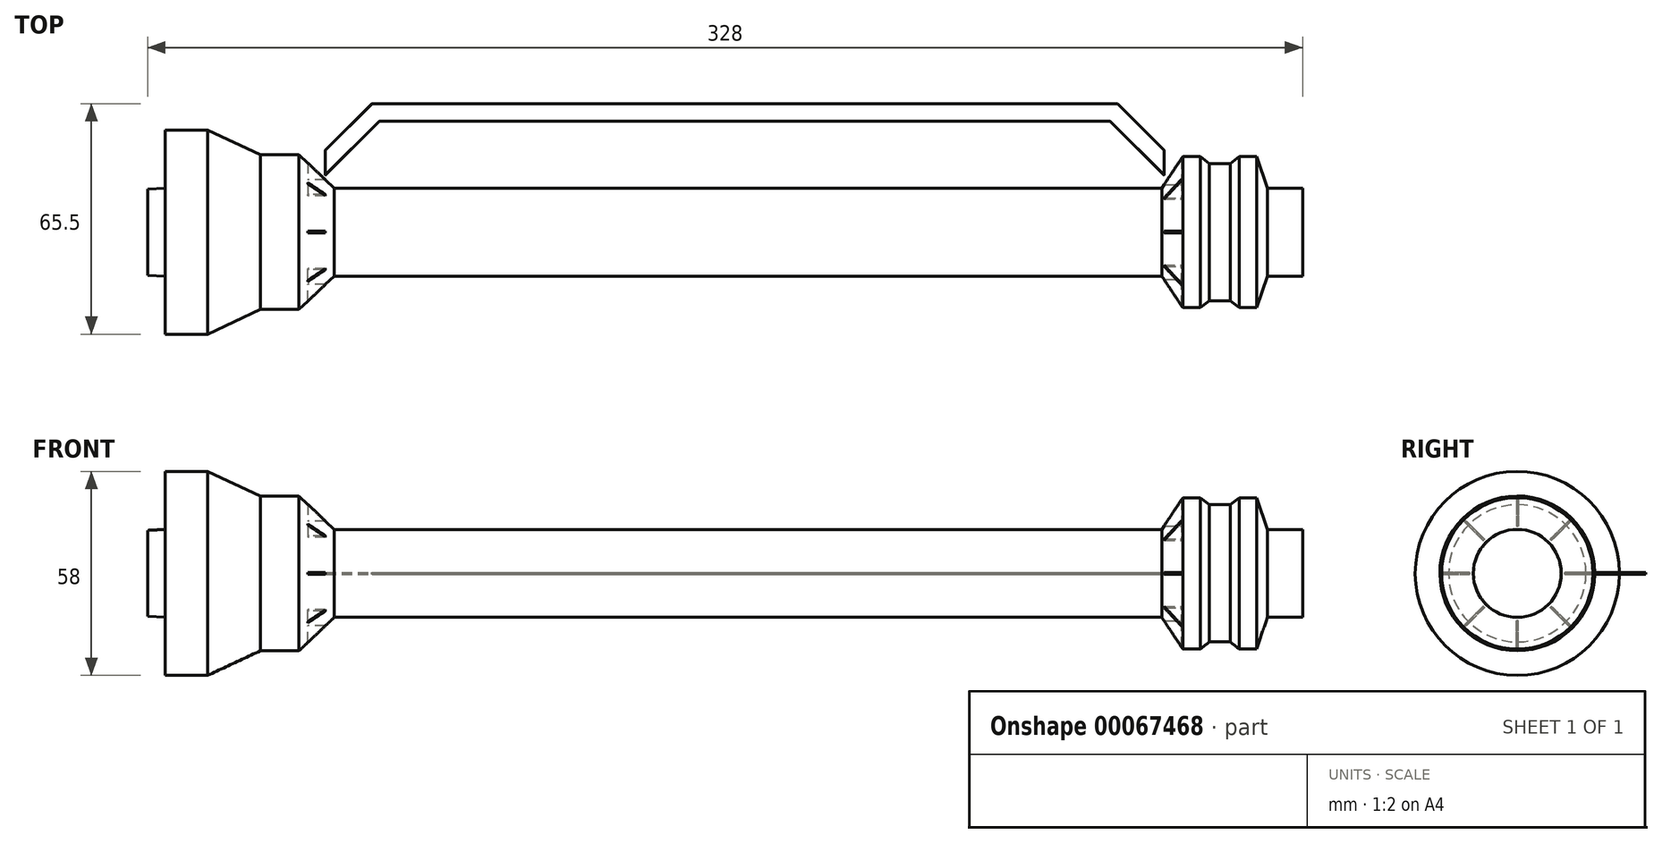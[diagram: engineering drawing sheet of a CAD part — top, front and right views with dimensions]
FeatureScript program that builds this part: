
annotation { "Feature Type Name" : "Feature", "Feature Type Description" : "" }
export const myFeature = defineFeature(function(context is Context, id is Id, definition is map)
    precondition{}
    {
        {
            assignVariable(context, id + "F0", {"name" : "s", "anyValue" : 1});
        }
        {
            var Q0;
            Q0=qCreatedBy(makeId("Top.planeOp"),FACE);
            var sketch = newSketch(context, id + "F1", { "sketchPlane" : qUnion([Q0])});
            skLineSegment(sketch, "E0", {"start": v(0, 0) * mm, "end": v(0, 29) * mm});
            skLineSegment(sketch, "E1", {"start": v(0, 29) * mm, "end": v(12, 29) * mm});
            skLineSegment(sketch, "E2", {"start": v(12, 29) * mm, "end": v(27, 22) * mm});
            skLineSegment(sketch, "E3", {"start": v(27, 22) * mm, "end": v(38, 22) * mm});
            skLineSegment(sketch, "E4", {"start": v(38, 22) * mm, "end": v(48, 12.5) * mm});
            skLineSegment(sketch, "E5", {"start": v(48, 12.5) * mm, "end": v(283, 12.5) * mm});
            skLineSegment(sketch, "E6", {"start": v(283, 12.5) * mm, "end": v(289, 21.5) * mm});
            skLineSegment(sketch, "E7", {"start": v(289, 21.5) * mm, "end": v(294, 21.5) * mm});
            skLineSegment(sketch, "E8", {"start": v(294, 21.5) * mm, "end": v(296.5, 19.5) * mm});
            skLineSegment(sketch, "E9", {"start": v(296.5, 19.5) * mm, "end": v(302.5, 19.5) * mm});
            skLineSegment(sketch, "E10", {"start": v(302.5, 19.5) * mm, "end": v(305, 21.5) * mm});
            skLineSegment(sketch, "E11", {"start": v(305, 21.5) * mm, "end": v(310, 21.5) * mm});
            skLineSegment(sketch, "E12", {"start": v(310, 21.5) * mm, "end": v(313, 12.5) * mm});
            skLineSegment(sketch, "E13", {"start": v(313, 12.5) * mm, "end": v(323, 12.5) * mm});
            skLineSegment(sketch, "E14", {"start": v(323, 12.5) * mm, "end": v(323, 0) * mm});
            skLineSegment(sketch, "E15", {"start": v(323, 0) * mm, "end": v(0, 0) * mm});
            skLineSegment(sketch, "E16", {"start": v(43, 17.25) * mm, "end": v(43, 14.87) * mm});
            skLineSegment(sketch, "E17", {"start": v(43, 14.87) * mm, "end": v(45.5, 14.87) * mm});
            skLineSegment(sketch, "E18", {"start": v(43, 14.87) * mm, "end": v(40.5, 14.87) * mm});
            skLineSegment(sketch, "E19", {"start": v(43, 17.25) * mm, "end": v(59.75, 34) * mm});
            skLineSegment(sketch, "E20", {"start": v(59.75, 34) * mm, "end": v(269.42, 34) * mm});
            skLineSegment(sketch, "E21", {"start": v(269.42, 34) * mm, "end": v(286.17, 17.25) * mm});
            skLineSegment(sketch, "E22", {"start": v(286.17, 17.25) * mm, "end": v(286.17, 13.5) * mm});
            skLineSegment(sketch, "E23", {"start": v(286.17, 13.5) * mm, "end": v(283.67, 13.5) * mm, "construction": true});
            skSolve(sketch);
        }
        {
            var Q0;
            Q0=makeQuery(id+"F1.imprint","IMPRINT",FACE,{"disambiguationData":[TD([[makeQuery(id+"F1.imprint","IMPRINT",EDGE,{"derivedFrom":sQuery(id+"F1.wireOp",EDGE,"E0")}),-1.0]])]});
            var Q1;
            {var subQ0=sQuery(id+"F1.wireOp",EDGE,"E16");Q1=makeQuery(id+"F1.imprint","IMPRINT",FACE,{"disambiguationData":[TD([[makeQuery(id+"F1.imprint","IMPRINT",EDGE,{"derivedFrom":subQ0}),1.0]])]});}
            var Q2;
            Q2=sQuery(id+"F1.wireOp",EDGE,"E15");
            revolve(context, id + "F2", {"entities" : qUnion([Q0, Q1]), "axis" : qUnion([Q2]), "revolveType" : RevolveType.SYMMETRIC, "angle" : 45 * degree});
        }
        {
            var Q0;
            Q0=sQuery(id+"F1.wireOp",EDGE,"E18");
            var Q1;
            Q1=sQuery(id+"F1.wireOp",EDGE,"E17");
            extrude(context, id + "F3", {"bodyType" : ToolBodyType.SURFACE, "surfaceEntities" : qUnion([Q0, Q1]), "endBound" : BoundingType.SYMMETRIC, "depth" : (0.5 * getVariable(context, 's')) * mm});
        }
        {
            var Q0;
            Q0=makeQuery(id+"F3.opExtrude","SWEPT_FACE",FACE,{"disambiguationData":[OSD([sQuery(id+"F1.wireOp",EDGE,"E17"),sQuery(id+"F1.wireOp",EDGE,"E18")])]});
            var sketch = newSketch(context, id + "F4", { "sketchPlane" : qUnion([Q0])});
            skCircle(sketch, "E24", {"center": v(-43, 0) * mm, "radius": 2.5 * mm});
            skPoint(sketch, "E24.centerSnap0", {"position": v(-45.5, 0) * mm});
            skPoint(sketch, "E24.centerSnap1", {"position": v(-43, 2.5) * mm});
            skSolve(sketch);
        }
        {
            var Q0;
            {var subQ0=sQuery(id+"F4.wireOp",EDGE,"E24");var subQ4=makeQuery(id+"F4.imprint","INTERSECT",VERTEX,{"derivedFrom":[makeQuery(id+"F3.opExtrude","SWEPT_EDGE",EDGE,{"disambiguationData":[OSD([sQuery(id+"F1.wireOp",VERTEX,"E18.end")])]}),subQ0]});Q0=makeQuery(id+"F4.imprint","IMPRINT",FACE,{"disambiguationData":[TD([[makeQuery(id+"F4.imprint","IMPRINT",EDGE,{"disambiguationData":[TD([[subQ4,-1.0]])],"derivedFrom":subQ0}),1.0]])]});}
            var Q1;
            Q1=sQuery(id+"F1.wireOp",EDGE,"E16");
            var Q2;
            Q2=sQuery(id+"F1.wireOp",EDGE,"E19");
            var Q3;
            Q3=sQuery(id+"F1.wireOp",EDGE,"E20");
            var Q4;
            Q4=sQuery(id+"F1.wireOp",EDGE,"E21");
            var Q5;
            Q5=sQuery(id+"F1.wireOp",EDGE,"E22");
            sweep(context, id + "F5", {"profiles" : qUnion([Q0]), "path" : qUnion([Q1, Q2, Q3, Q4, Q5])});
        }
        {
            var Q0;
            Q0=makeQuery(id+"F5.opSweep","CAP_FACE",FACE,{"disambiguationData":[OSD([sQuery(id+"F1.wireOp",VERTEX,"E16.end"),sQuery(id+"F4.wireOp",EDGE,"E24")])],"isStart":true});
            var Q1;
            Q1=makeQuery(id+"F5.opSweep","CAP_FACE",FACE,{"disambiguationData":[OSD([sQuery(id+"F1.wireOp",VERTEX,"E22.end"),sQuery(id+"F4.wireOp",EDGE,"E24")])],"isStart":false});
            extrude(context, id + "F6", {"entities" : qUnion([Q0, Q1]), "operationType" : NewBodyOperationType.REMOVE, "endBound" : BoundingType.THROUGH_ALL, "oppositeDirection" : true, "depth" : 25 * mm});
        }
        {
            var Q0;
            Q0=makeQuery(id+"F2.opRevolve","SWEPT_BODY",BODY,{"disambiguationData":[OSD([sQuery(id+"F1.wireOp",EDGE,"E0"),sQuery(id+"F1.wireOp",EDGE,"E1"),sQuery(id+"F1.wireOp",EDGE,"E2"),sQuery(id+"F1.wireOp",EDGE,"E3"),sQuery(id+"F1.wireOp",EDGE,"E4"),sQuery(id+"F1.wireOp",EDGE,"E5"),sQuery(id+"F1.wireOp",EDGE,"E6"),sQuery(id+"F1.wireOp",EDGE,"E7"),sQuery(id+"F1.wireOp",EDGE,"E8"),sQuery(id+"F1.wireOp",EDGE,"E9"),sQuery(id+"F1.wireOp",EDGE,"E10"),sQuery(id+"F1.wireOp",EDGE,"E11"),sQuery(id+"F1.wireOp",EDGE,"E12"),sQuery(id+"F1.wireOp",EDGE,"E13"),sQuery(id+"F1.wireOp",EDGE,"E14"),sQuery(id+"F1.wireOp",EDGE,"E15")])]});
            var Q1;
            Q1=makeQuery(id+"F2.opRevolve","CAP_EDGE",EDGE,{"disambiguationData":[OSD([sQuery(id+"F1.wireOp",EDGE,"E15")])],"isStart":true});
            circularPattern(context, id + "F7", {"operationType" : NewBodyOperationType.ADD, "entities" : qUnion([Q0]), "axis" : qUnion([Q1]), "angle" : 360 * degree, "instanceCount" : 8, "equalSpace" : true});
        }
        {
            var Q0;
            {var subQ0=makeQuery(id+"F2.opRevolve","SWEPT_FACE",FACE,{"disambiguationData":[OSD([sQuery(id+"F1.wireOp",EDGE,"E0")])]});Q0=makeQuery(id+"F7.boolean.opBoolean","MERGE",FACE,{"derivedFrom":[subQ0,makeQuery(id+"F7.opPattern","COPY",FACE,{"derivedFrom":subQ0,"instanceName":"1"}),makeQuery(id+"F7.opPattern","COPY",FACE,{"derivedFrom":subQ0,"instanceName":"2"}),makeQuery(id+"F7.opPattern","COPY",FACE,{"derivedFrom":subQ0,"instanceName":"3"}),makeQuery(id+"F7.opPattern","COPY",FACE,{"derivedFrom":subQ0,"instanceName":"4"}),makeQuery(id+"F7.opPattern","COPY",FACE,{"derivedFrom":subQ0,"instanceName":"5"}),makeQuery(id+"F7.opPattern","COPY",FACE,{"derivedFrom":subQ0,"instanceName":"6"}),makeQuery(id+"F7.opPattern","COPY",FACE,{"derivedFrom":subQ0,"instanceName":"7"})]});}
            var sketch = newSketch(context, id + "F8", { "sketchPlane" : qUnion([Q0])});
            skCircle(sketch, "E25.0", {"center": v(0, 0) * mm, "radius": 12.5 * mm});
            skSolve(sketch);
        }
        {
            var Q0;
            Q0 = qSketchRegion(id + "F8", true);
            extrude(context, id + "F9", {"entities" : qUnion([Q0]), "operationType" : NewBodyOperationType.ADD, "depth" : (5 * getVariable(context, 's')) * mm, "hasDraft" : true, "draftAngle" : 3 * degree, "draftPullDirection" : true});
        }
        {
            assignVariable(context, id + "F10", {"name" : "scale", "anyValue" : 1});
        }
        {
            var Q0;
            Q0=makeQuery(id+"F2.opRevolve","SWEPT_BODY",BODY,{"disambiguationData":[OSD([sQuery(id+"F1.wireOp",EDGE,"E0"),sQuery(id+"F1.wireOp",EDGE,"E1"),sQuery(id+"F1.wireOp",EDGE,"E2"),sQuery(id+"F1.wireOp",EDGE,"E3"),sQuery(id+"F1.wireOp",EDGE,"E4"),sQuery(id+"F1.wireOp",EDGE,"E5"),sQuery(id+"F1.wireOp",EDGE,"E6"),sQuery(id+"F1.wireOp",EDGE,"E7"),sQuery(id+"F1.wireOp",EDGE,"E8"),sQuery(id+"F1.wireOp",EDGE,"E9"),sQuery(id+"F1.wireOp",EDGE,"E10"),sQuery(id+"F1.wireOp",EDGE,"E11"),sQuery(id+"F1.wireOp",EDGE,"E12"),sQuery(id+"F1.wireOp",EDGE,"E13"),sQuery(id+"F1.wireOp",EDGE,"E14"),sQuery(id+"F1.wireOp",EDGE,"E15")])]});
            var Q1;
            Q1=makeQuery(id+"F5.opSweep","SWEPT_BODY",BODY,{"disambiguationData":[OSD([sQuery(id+"F1.wireOp",EDGE,"E22"),sQuery(id+"F4.wireOp",EDGE,"E24")])]});
            var Q2;
            Q2=qCreatedBy(makeId("Origin.pointOp"),VERTEX);
            transform(context, id + "F11", {"entities" : qUnion([Q0, Q1]), "transformType" : TransformType.SCALE_UNIFORMLY, "scale" : getVariable(context, 'scale'), "scalePoint" : qUnion([Q2]), "makeCopy" : false});
        }
    });
